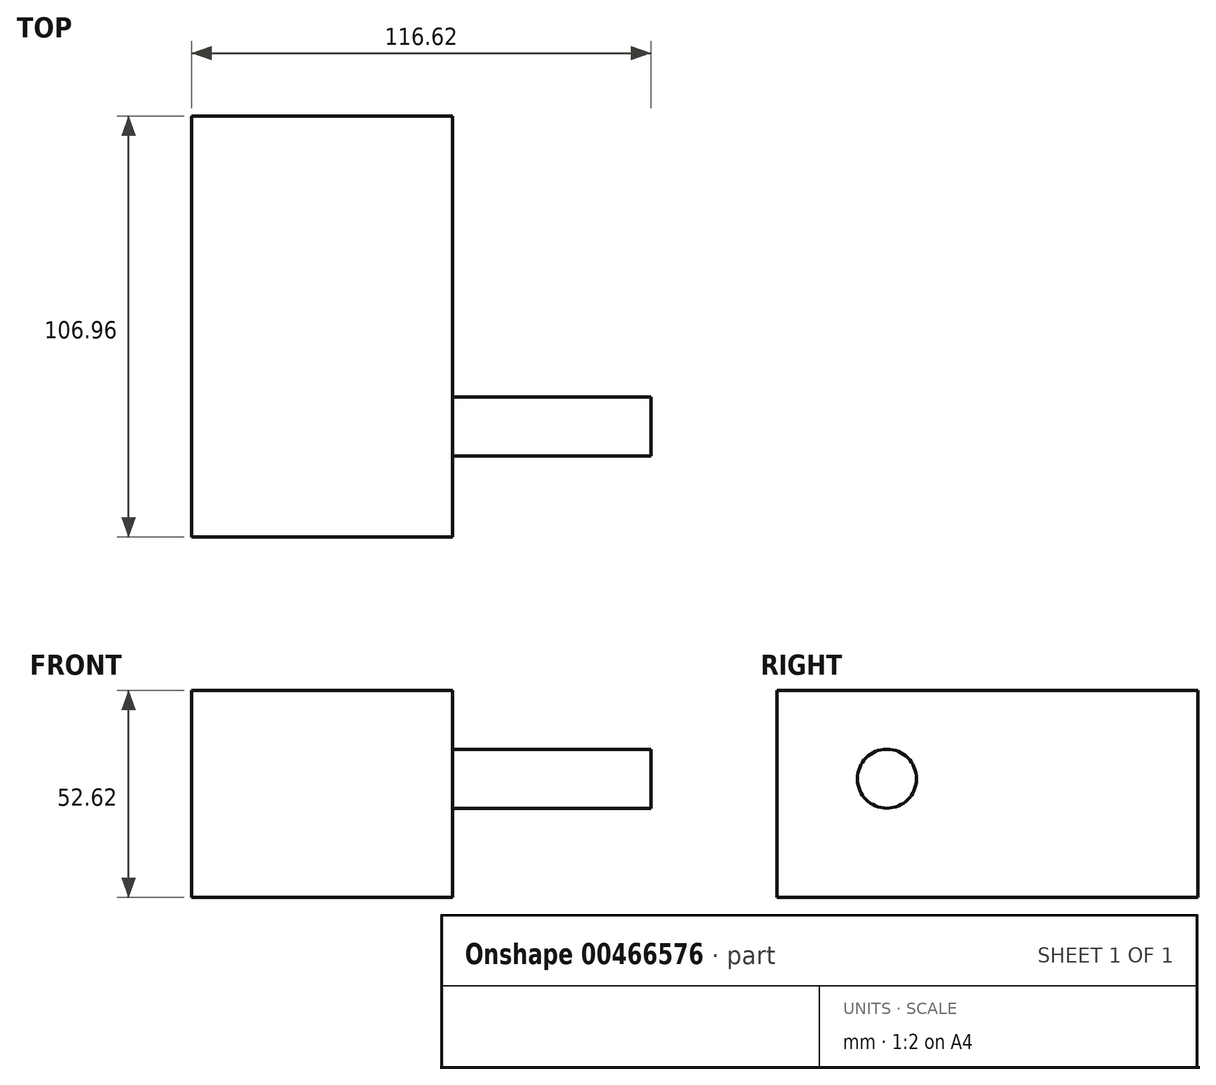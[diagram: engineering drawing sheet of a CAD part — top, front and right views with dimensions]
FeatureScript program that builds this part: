
annotation { "Feature Type Name" : "Feature", "Feature Type Description" : "" }
export const myFeature = defineFeature(function(context is Context, id is Id, definition is map)
    precondition{}
    {
        {
            var Q0;
            Q0=qCreatedBy(makeId("Front.planeOp"),FACE);
            var sketch = newSketch(context, id + "F0", { "sketchPlane" : qUnion([Q0])});
            skLineSegment(sketch, "E0.bottom", {"start": v(-32.52, 26.18) * mm, "end": v(33.72, 26.18) * mm});
            skLineSegment(sketch, "E0.top", {"start": v(-32.52, -26.44) * mm, "end": v(33.72, -26.44) * mm});
            skLineSegment(sketch, "E0.left", {"start": v(-32.52, 26.18) * mm, "end": v(-32.52, -26.44) * mm});
            skLineSegment(sketch, "E0.right", {"start": v(33.72, 26.18) * mm, "end": v(33.72, -26.44) * mm});
            skSolve(sketch);
        }
        {
            var Q0;
            Q0=makeQuery(id+"F0.imprint","IMPRINT",FACE,{"disambiguationData":[TD([[makeQuery(id+"F0.imprint","IMPRINT",EDGE,{"derivedFrom":sQuery(id+"F0.wireOp",EDGE,"E0.bottom")}),-1.0]])]});
            extrude(context, id + "F1", {"entities" : qUnion([Q0]), "depth" : 53.9 * mm});
        }
        {
            var Q0;
            Q0 = qSketchRegion(id + "FvOdJRGyPNqfMgk_1", true);
            var Q1;
            Q1=makeQuery(id+"F1.opExtrude","CAP_FACE",FACE,{"disambiguationData":[OSD([sQuery(id+"F0.wireOp",EDGE,"E0.bottom"),sQuery(id+"F0.wireOp",EDGE,"E0.top"),sQuery(id+"F0.wireOp",EDGE,"E0.left"),sQuery(id+"F0.wireOp",EDGE,"E0.right")])],"isStart":true});
            extrude(context, id + "F2", {"entities" : qUnion([Q0, Q1]), "operationType" : NewBodyOperationType.ADD, "depth" : 53.05 * mm});
        }
        {
            var Q0;
            Q0=qCreatedBy(makeId("Right.planeOp"),FACE);
            var sketch = newSketch(context, id + "F3", { "sketchPlane" : qUnion([Q0])});
            skCircle(sketch, "E1", {"center": v(-25.9, 3.75) * mm, "radius": 7.5 * mm});
            skSolve(sketch);
        }
        {
            var Q0;
            Q0 = qSketchRegion(id + "F3", true);
            extrude(context, id + "F4", {"entities" : qUnion([Q0]), "operationType" : NewBodyOperationType.ADD, "depth" : 84.1 * mm});
        }
        {
            var Q0;
            Q0=qCreatedBy(makeId("Front.planeOp"),FACE);
            var sketch = newSketch(context, id + "F5", { "sketchPlane" : qUnion([Q0])});
            skLineSegment(sketch, "E2.bottom", {"start": v(33.3, -22.1) * mm, "end": v(24.12, -22.1) * mm});
            skLineSegment(sketch, "E2.top", {"start": v(33.3, -12.64) * mm, "end": v(24.12, -12.64) * mm});
            skLineSegment(sketch, "E2.left", {"start": v(33.3, -22.1) * mm, "end": v(33.3, -12.64) * mm});
            skLineSegment(sketch, "E2.right", {"start": v(24.12, -22.1) * mm, "end": v(24.12, -12.64) * mm});
            skSolve(sketch);
        }
    });
